# Revit family: Haworth_Janus_GigiII_CocoonChair
name_source: partatom
category: Furniture
revit_build: Autodesk Revit 2018 (Build: 20170223_1515(x64)
units: mm (PartAtom-declared; Revit-internal decimal feet)

## family parameters
Always vertical = Yes
Cut with Voids When Loaded = No
OmniClass Number = 23.40.70.14.64.21
OmniClass Title = Systems Furniture
Room Calculation Point = No
Shared = No
Work Plane-Based = No

## types (1)
- HCJC-GG-L1 - Cocoon Chair
    Actual Depth = 32 3/4"
    Actual Height = 35"
    Actual Width = 38 1/2"
    Assembly Code = E2020200
    Description = Haworth - Gigi II - Cocoon Chair
    Glide Finish = Haworth _ Polymer _ Slate
    Manufacturer = Haworth
    Model = HCJC-GG-L1
    Revision Number = 1
    Size = Verify Final Dim. w/ Haworth
    Sustainability Info = https://www.haworth.com
    URL = http://www.haworth.com
    URL - Product = https://www.haworth.com
    Warranty = http://www.haworth.com
    With Pillows = Yes
    With Seat Cushion = Yes

## geometry (parser evidence)
native form markers: Sweep x5
no freeform markers — native parametric forms only
